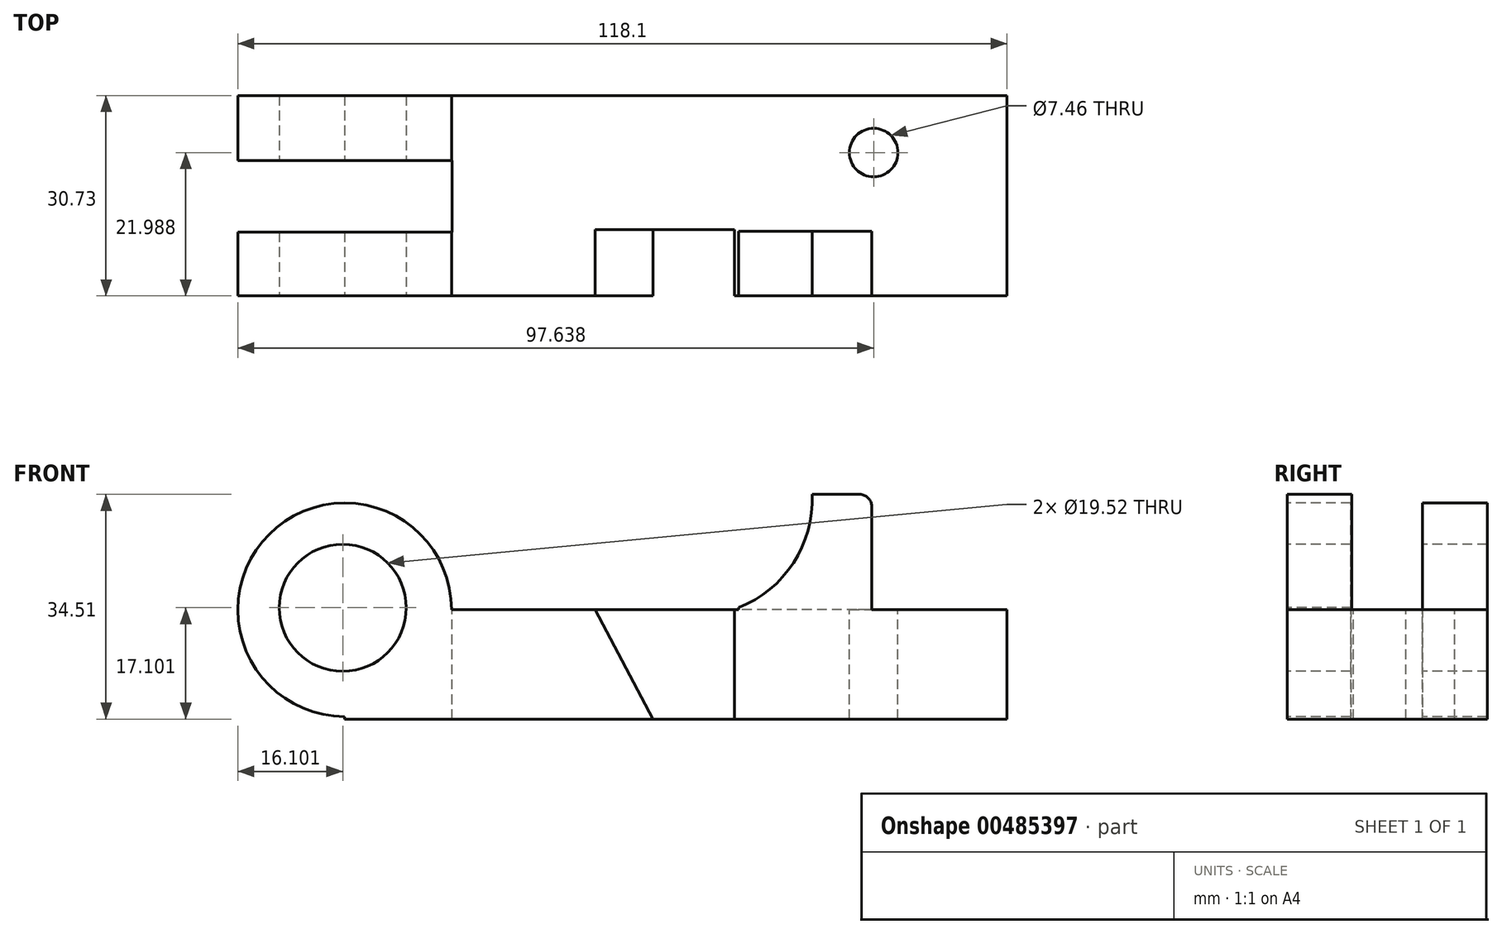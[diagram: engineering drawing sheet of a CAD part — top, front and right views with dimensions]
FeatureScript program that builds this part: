
annotation { "Feature Type Name" : "Feature", "Feature Type Description" : "" }
export const myFeature = defineFeature(function(context is Context, id is Id, definition is map)
    precondition{}
    {
        {
            var Q0;
            Q0=qCreatedBy(makeId("Front.planeOp"),FACE);
            var sketch = newSketch(context, id + "F0", { "sketchPlane" : qUnion([Q0])});
            skCircle(sketch, "E0", {"center": v(-30.84, 16.8) * mm, "radius": 16.4 * mm});
            skLineSegment(sketch, "E1.bottom", {"start": v(-30.84, 16.8) * mm, "end": v(70.85, 16.8) * mm});
            skLineSegment(sketch, "E1.top", {"start": v(-30.84, 0) * mm, "end": v(70.85, 0) * mm});
            skLineSegment(sketch, "E1.left", {"start": v(-30.84, 16.8) * mm, "end": v(-30.84, 0) * mm});
            skLineSegment(sketch, "E1.right", {"start": v(70.85, 16.8) * mm, "end": v(70.85, 0) * mm});
            skSolve(sketch);
        }
        {
            var Q0;
            {var subQ0=sQuery(id+"F0.wireOp",EDGE,"E1.bottom");var subQ1=sQuery(id+"F0.wireOp",EDGE,"E0");var subQ2=makeQuery(id+"F0.imprint","INTERSECT",VERTEX,{"derivedFrom":[subQ1,subQ0]});Q0=makeQuery(id+"F0.imprint","IMPRINT",FACE,{"disambiguationData":[TD([[makeQuery(id+"F0.imprint","IMPRINT",EDGE,{"disambiguationData":[TD([[subQ2,-1.0]])],"derivedFrom":subQ1}),1.0]])]});}
            var Q1;
            {var subQ0=sQuery(id+"F0.wireOp",EDGE,"E1.bottom");var subQ1=sQuery(id+"F0.wireOp",EDGE,"E0");var subQ2=makeQuery(id+"F0.imprint","INTERSECT",VERTEX,{"derivedFrom":[subQ1,subQ0]});Q1=makeQuery(id+"F0.imprint","IMPRINT",FACE,{"disambiguationData":[TD([[makeQuery(id+"F0.imprint","IMPRINT",EDGE,{"disambiguationData":[TD([[subQ2,1.0]])],"derivedFrom":subQ1}),1.0]])]});}
            var Q2;
            {var subQ0=sQuery(id+"F0.wireOp",EDGE,"E1.top");Q2=makeQuery(id+"F0.imprint","IMPRINT",FACE,{"disambiguationData":[TD([[makeQuery(id+"F0.imprint","IMPRINT",EDGE,{"derivedFrom":subQ0}),1.0]])]});}
            extrude(context, id + "F1", {"entities" : qUnion([Q0, Q1, Q2]), "oppositeDirection" : true, "depth" : 30.73 * mm});
        }
        {
            var Q0;
            Q0=qCreatedBy(makeId("Top.planeOp"),FACE);
            cPlane(context, id + "F2", {"entities" : qUnion([Q0]), "cplaneType" : CPlaneType.OFFSET, "offset" : 34.3 * mm, "width" : 152.4 * mm, "height" : 152.4 * mm});
        }
        {
            var Q0;
            Q0=qCreatedBy(id+"F2.planeOp",FACE);
            var sketch = newSketch(context, id + "F3", { "sketchPlane" : qUnion([Q0])});
            skLineSegment(sketch, "E2.bottom", {"start": v(-47.33, 20.77) * mm, "end": v(-14.35, 20.77) * mm});
            skLineSegment(sketch, "E2.top", {"start": v(-47.33, 9.77) * mm, "end": v(-14.35, 9.77) * mm});
            skLineSegment(sketch, "E2.left", {"start": v(-47.33, 20.77) * mm, "end": v(-47.33, 9.77) * mm});
            skLineSegment(sketch, "E2.right", {"start": v(-14.35, 20.77) * mm, "end": v(-14.35, 9.77) * mm});
            skSolve(sketch);
        }
        {
            var Q0;
            Q0 = qSketchRegion(id + "F3", true);
            extrude(context, id + "F4", {"entities" : qUnion([Q0]), "operationType" : NewBodyOperationType.REMOVE, "oppositeDirection" : true, "depth" : 53.85 * mm});
        }
        {
            var Q0;
            Q0=qCreatedBy(makeId("Front.planeOp"),FACE);
            var sketch = newSketch(context, id + "F5", { "sketchPlane" : qUnion([Q0])});
            skCircle(sketch, "E3", {"center": v(-31.15, 17.1) * mm, "radius": 9.76 * mm});
            skSolve(sketch);
        }
        {
            var Q0;
            Q0 = qSketchRegion(id + "F5", true);
            var Q1;
            Q1=sQuery(id+"F5.wireOp",EDGE,"E3");
            extrude(context, id + "F6", {"entities" : qUnion([Q0]), "operationType" : NewBodyOperationType.REMOVE, "surfaceEntities" : qUnion([Q1]), "oppositeDirection" : true, "depth" : 53.1 * mm});
        }
        {
            var Q0;
            Q0=qCreatedBy(makeId("Front.planeOp"),FACE);
            var sketch = newSketch(context, id + "F7", { "sketchPlane" : qUnion([Q0])});
            skLineSegment(sketch, "E4", {"start": v(29.62, 0) * mm, "end": v(29.62, 17.1) * mm});
            skArc(sketch, "E5", {"start": v(29.62, 17.1) * mm, "mid": v(38.06, 24) * mm, "end": v(40.92, 34.5) * mm});
            skLineSegment(sketch, "E6", {"start": v(40.92, 34.5) * mm, "end": v(50.08, 34.5) * mm});
            skLineSegment(sketch, "E7", {"start": v(50.08, 34.5) * mm, "end": v(50.08, 0) * mm});
            skLineSegment(sketch, "E8", {"start": v(50.08, 0) * mm, "end": v(29.62, 0) * mm});
            skSolve(sketch);
        }
        {
            var Q0;
            Q0=makeQuery(id+"F7.imprint","IMPRINT",FACE,{"disambiguationData":[TD([[makeQuery(id+"F7.imprint","IMPRINT",EDGE,{"derivedFrom":sQuery(id+"F7.wireOp",EDGE,"E4")}),-1.0]])]});
            extrude(context, id + "F8", {"entities" : qUnion([Q0]), "operationType" : NewBodyOperationType.ADD, "oppositeDirection" : true, "depth" : 9.9 * mm});
        }
        {
            var Q0;
            Q0=makeQuery(id+"F8.opExtrude","SWEPT_EDGE",EDGE,{"disambiguationData":[OSD([sQuery(id+"F7.wireOp",EDGE,"E6"),sQuery(id+"F7.wireOp",EDGE,"E7")])]});
            fillet(context, id + "F9", {"entities" : qUnion([Q0]), "radius" : 1.84 * mm, "tangentPropagation" : true, "allowEdgeOverflow" : false});
        }
        {
            var Q0;
            Q0=qCreatedBy(makeId("Front.planeOp"),FACE);
            var sketch = newSketch(context, id + "F10", { "sketchPlane" : qUnion([Q0])});
            skLineSegment(sketch, "E9", {"start": v(29.01, 17.1) * mm, "end": v(29.01, 0) * mm});
            skLineSegment(sketch, "E10", {"start": v(29.01, 0) * mm, "end": v(16.5, 0) * mm});
            skLineSegment(sketch, "E11", {"start": v(16.5, 0) * mm, "end": v(7.63, 16.8) * mm});
            skLineSegment(sketch, "E12", {"start": v(7.63, 16.8) * mm, "end": v(29.01, 17.1) * mm});
            skSolve(sketch);
        }
        {
            var Q0;
            Q0 = qSketchRegion(id + "F10", true);
            extrude(context, id + "F11", {"entities" : qUnion([Q0]), "operationType" : NewBodyOperationType.REMOVE, "oppositeDirection" : true, "depth" : 10.16 * mm});
        }
        {
            var Q0;
            Q0=makeQuery(id+"F1.opExtrude","SWEPT_FACE",FACE,{"disambiguationData":[OSD([sQuery(id+"F0.wireOp",EDGE,"E1.bottom")])]});
            var sketch = newSketch(context, id + "F12", { "sketchPlane" : qUnion([Q0])});
            skCircle(sketch, "E13", {"center": v(50.39, 21.99) * mm, "radius": 3.73 * mm});
            skSolve(sketch);
        }
        {
            var Q0;
            Q0 = qSketchRegion(id + "F12", true);
            extrude(context, id + "F13", {"entities" : qUnion([Q0]), "operationType" : NewBodyOperationType.REMOVE, "oppositeDirection" : true, "depth" : 25.4 * mm});
        }
    });
